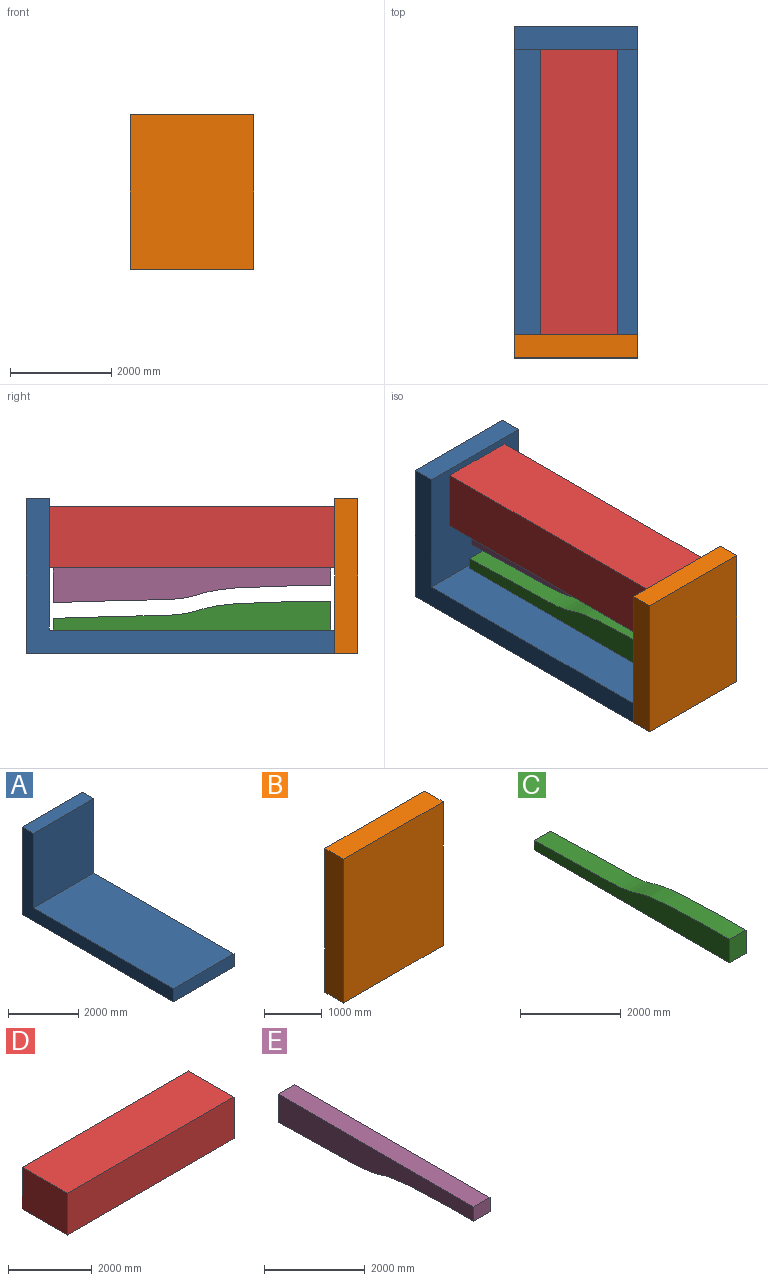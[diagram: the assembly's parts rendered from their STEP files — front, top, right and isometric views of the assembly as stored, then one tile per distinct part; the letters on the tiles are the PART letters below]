
ASSEMBLY  parts=5 mates=4
PART A: 8 faces, bbox 2438.4x6096x3048 mm
  f0: plane 2590.8x2438.4mm, normal (0,-1,0), area 6317406.7mm2, adj f1,f2,f4,f7
  f1: plane 6096x3048mm, normal (-1,0,0), area 3971605mm2, adj f0,f3,f4,f5,f6,f7
  f2: plane 6096x3048mm, normal (1,0,0), area 3971605mm2, adj f0,f3,f4,f5,f6,f7
  f3: plane 3048x2438.4mm, normal (0,1,0), area 7432243.2mm2, adj f1,f2,f4,f5
  f4: plane 2438.4x457.2mm, normal (0,0,1), area 1114836.5mm2, adj f0,f1,f2,f3
  f5: plane 6096x2438.4mm, normal (0,0,-1), area 14864486.4mm2, adj f1,f2,f3,f6
  f6: plane 2438.4x457.2mm, normal (0,-1,0), area 1114836.5mm2, adj f1,f2,f5,f7
  f7: plane 5638.8x2438.4mm, normal (0,0,1), area 13749649.9mm2, adj f0,f1,f2,f6
PART B: 6 faces, bbox 2438.4x457.2x3048 mm
  f0: plane 3048x457.2mm, normal (-1,0,0), area 1393545.6mm2, adj f1,f3,f4,f5
  f1: plane 3048x2438.4mm, normal (0,-1,0), area 7432243.2mm2, adj f0,f2,f4,f5
  f2: plane 3048x457.2mm, normal (1,0,0), area 1393545.6mm2, adj f1,f3,f4,f5
  f3: plane 3048x2438.4mm, normal (0,1,0), area 7432243.2mm2, adj f0,f2,f4,f5
  f4: plane 2438.4x457.2mm, normal (0,0,1), area 1114836.5mm2, adj f0,f1,f2,f3
  f5: plane 2438.4x457.2mm, normal (0,0,-1), area 1114836.5mm2, adj f0,f1,f2,f3
PART C: 6 faces, bbox 457.2x5486.4x577 mm
  f0: plane 567.59x457.2mm, normal (0,-1,0), area 259500.7mm2, adj f1,f3,f4,f5
  f1: plane 5486.4x457.2mm, normal (0,0,-1), area 2508382.1mm2, adj f0,f2,f4,f5
  f2: plane 457.2x230.03mm, normal (0,1,0), area 105169mm2, adj f1,f3,f4,f5
  f3: extruded ~5486.4x457.2mm, area 2521890.1mm2, adj f0,f2,f4,f5
  f4: plane 5486.4x576.98mm, normal (1,0,0), area 2178380.6mm2, adj f0,f1,f2,f3
  f5: plane 5486.4x576.98mm, normal (-1,0,0), area 2178380.6mm2, adj f0,f1,f2,f3
PART D: 6 faces, bbox 5638.8x1524x1219.2 mm
  f0: plane 1524x1219.2mm, normal (-1,0,0), area 1858060.8mm2, adj f1,f3,f4,f5
  f1: plane 5638.8x1219.2mm, normal (0,-1,0), area 6874825mm2, adj f0,f2,f4,f5
  f2: plane 1524x1219.2mm, normal (1,0,0), area 1858060.8mm2, adj f1,f3,f4,f5
  f3: plane 5638.8x1219.2mm, normal (0,1,0), area 6874825mm2, adj f0,f2,f4,f5
  f4: plane 5638.8x1524mm, normal (0,0,1), area 8593531.2mm2, adj f0,f1,f2,f3
  f5: plane 5638.8x1524mm, normal (0,0,-1), area 8593531.2mm2, adj f0,f1,f2,f3
PART E: 6 faces, bbox 457.2x5486.4x685.6 mm
  f0: plane 457.2x346.81mm, normal (0,-1,0), area 158562.9mm2, adj f1,f3,f4,f5
  f1: extruded ~5486.4x457.2mm, area 2521890.1mm2, adj f0,f2,f4,f5
  f2: plane 684.37x457.2mm, normal (0,1,0), area 312894.6mm2, adj f1,f3,f4,f5
  f3: plane 5486.4x457.2mm, normal (0,0,1), area 2508382.1mm2, adj f0,f2,f4,f5
  f4: plane 5486.4x685.56mm, normal (1,0,0), area 2838383.5mm2, adj f0,f1,f2,f3
  f5: plane 5486.4x685.56mm, normal (-1,0,0), area 2838383.5mm2, adj f0,f1,f2,f3
PLACE A t=(-2438.4,0,0)mm
PLACE B t=(-2438.4,0,0)mm
PLACE C t=(-1447.8,533.4,457.2)mm
PLACE D rot(axis=(0,0,1),90deg) t=(-403.12,457.2,1683.45)mm
PLACE E t=(-1393.72,533.4,769.05)mm
MATE fastened C.f1 <-> A.f7  axis (0,0,-1) through (-1219.2,3276.6,457.2)mm
MATE fastened E.f3 <-> D.f5  axis (0,0,1) through (-1165.12,3276.6,1683.45)mm
MATE planar B.f3 <-> D.f0  axis (0,1,0) through (-1219.2,457.2,1524)mm
MATE fastened A.f5 <-> B.f5  axis (0,0,1) through (0,457.2,0)mm
